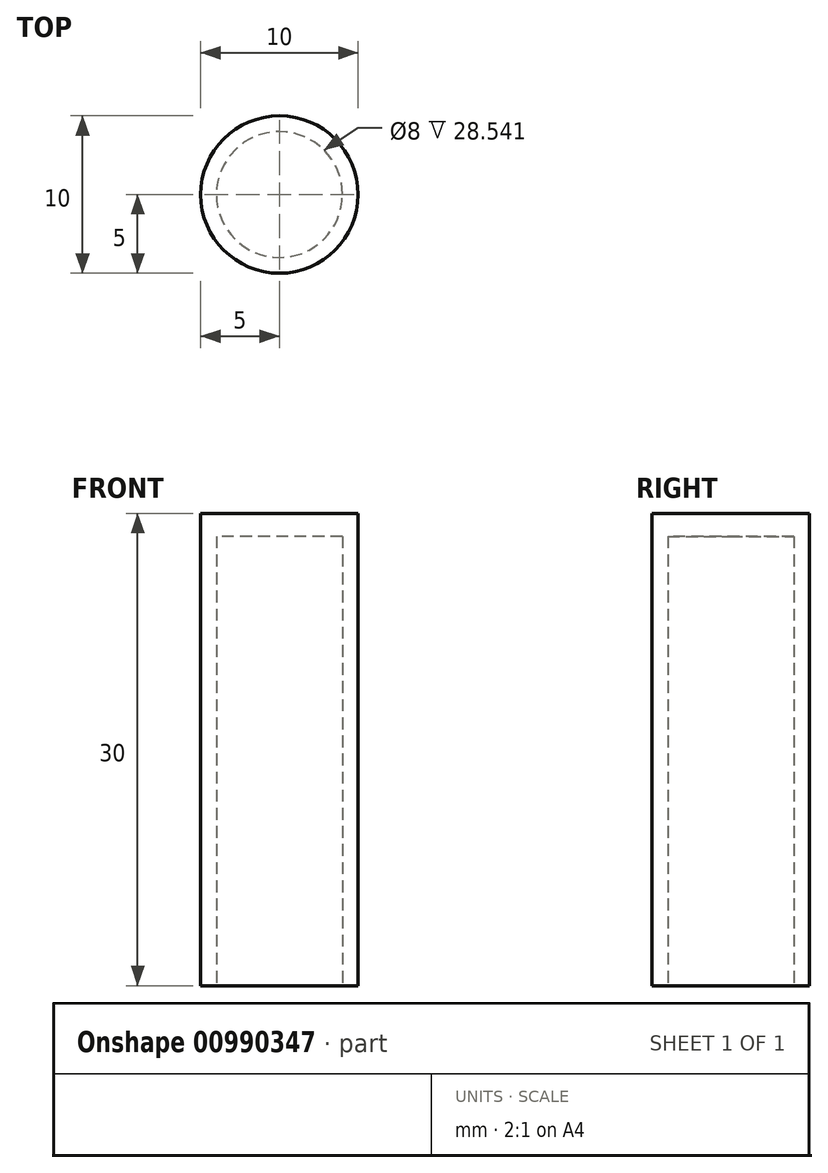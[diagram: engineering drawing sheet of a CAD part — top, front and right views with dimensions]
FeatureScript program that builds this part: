
annotation { "Feature Type Name" : "Feature", "Feature Type Description" : "" }
export const myFeature = defineFeature(function(context is Context, id is Id, definition is map)
    precondition{}
    {
        {
            var Q0;
            Q0=qCreatedBy(makeId("Top.planeOp"),FACE);
            var sketch = newSketch(context, id + "F0", { "sketchPlane" : qUnion([Q0])});
            skCircle(sketch, "E0", {"center": v(0, 0) * mm, "radius": 5 * mm});
            skSolve(sketch);
        }
        {
            var Q0;
            Q0=makeQuery(id+"F0.imprint","IMPRINT",FACE,{"disambiguationData":[TD([[makeQuery(id+"F0.imprint","IMPRINT",EDGE,{"derivedFrom":sQuery(id+"F0.wireOp",EDGE,"E0")}),1.0]])]});
            var Q1;
            Q1 = qSketchRegion(id + "Fi8k8hFmVNHmTET_0", true);
            extrude(context, id + "F1", {"entities" : qUnion([Q0, Q1]), "depth" : 30 * mm, "offsetDistance" : 25 * mm});
        }
        {
            var Q0;
            Q0=makeQuery(id+"F0.imprint","IMPRINT",FACE,{"disambiguationData":[TD([[makeQuery(id+"F0.imprint","IMPRINT",EDGE,{"derivedFrom":sQuery(id+"F0.wireOp",EDGE,"E0")}),1.0]])]});
            var sketch = newSketch(context, id + "F2", { "sketchPlane" : qUnion([Q0])});
            skCircle(sketch, "E1", {"center": v(0, 0) * mm, "radius": 4 * mm});
            skSolve(sketch);
        }
        {
            var Q0;
            Q0=makeQuery(id+"F2.imprint","IMPRINT",FACE,{"disambiguationData":[TD([[makeQuery(id+"F2.imprint","IMPRINT",EDGE,{"derivedFrom":sQuery(id+"F2.wireOp",EDGE,"E1")}),1.0]])]});
            extrude(context, id + "F3", {"entities" : qUnion([Q0]), "operationType" : NewBodyOperationType.REMOVE, "depth" : 28.54 * mm, "offsetDistance" : 25 * mm});
        }
    });
